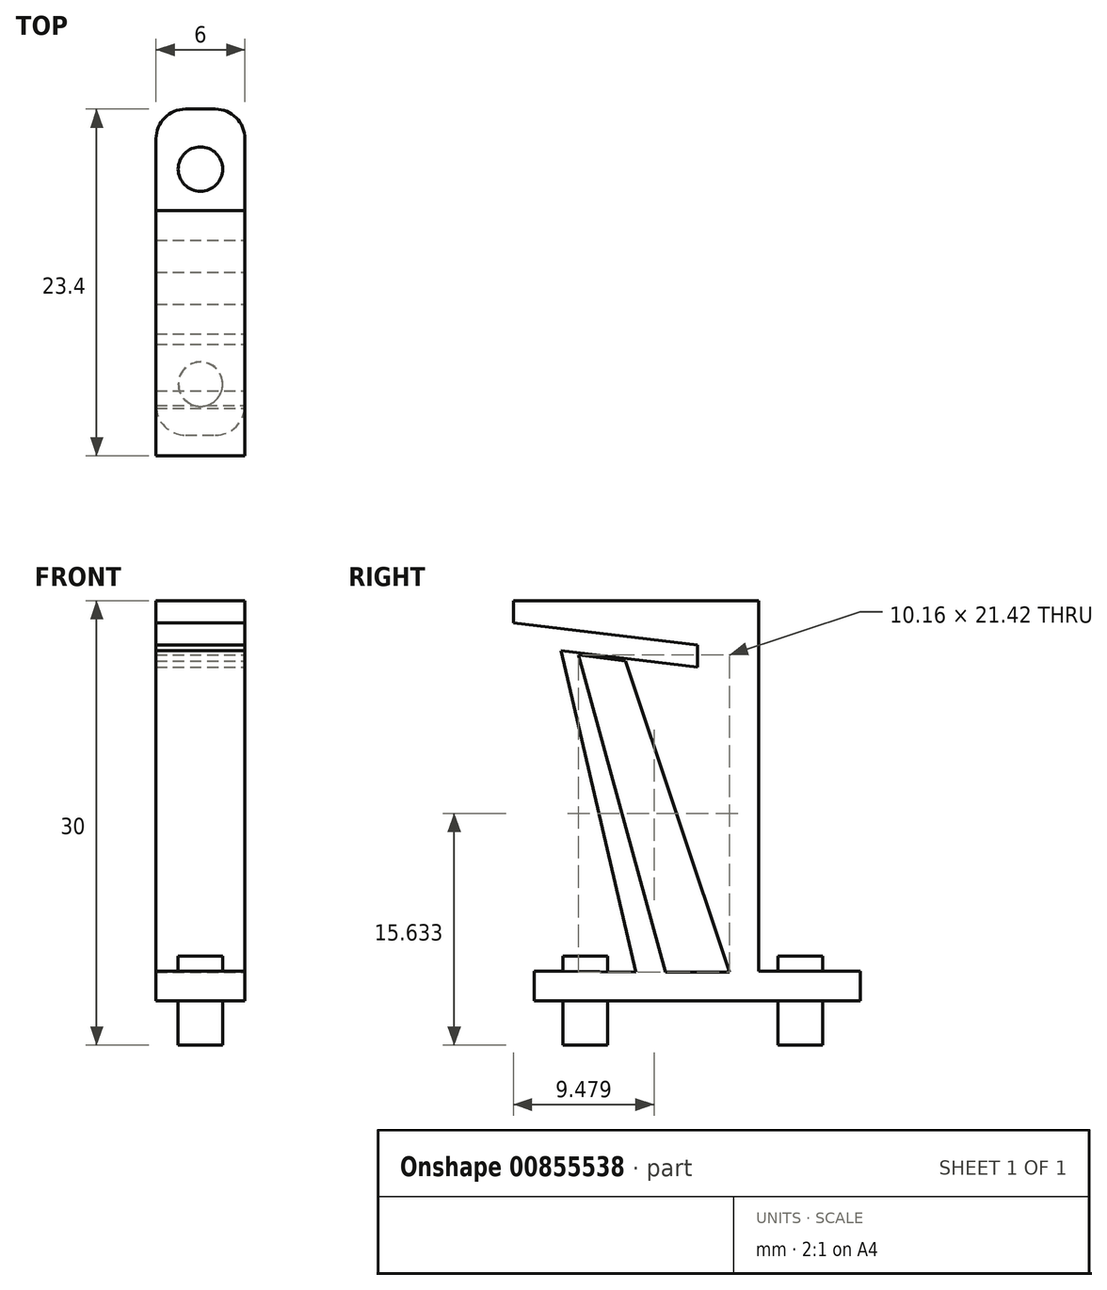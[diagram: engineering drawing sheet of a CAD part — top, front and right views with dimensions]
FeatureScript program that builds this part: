
annotation { "Feature Type Name" : "Feature", "Feature Type Description" : "" }
export const myFeature = defineFeature(function(context is Context, id is Id, definition is map)
    precondition{}
    {
        {
            var Q0;
            Q0=qCreatedBy(makeId("Top.planeOp"),FACE);
            var sketch = newSketch(context, id + "F0", { "sketchPlane" : qUnion([Q0])});
            skLineSegment(sketch, "E0.bottom", {"start": v(-3, 11) * mm, "end": v(3, 11) * mm});
            skLineSegment(sketch, "E0.top", {"start": v(-3, -11) * mm, "end": v(3, -11) * mm});
            skLineSegment(sketch, "E0.left", {"start": v(-3, 11) * mm, "end": v(-3, -11) * mm});
            skLineSegment(sketch, "E0.right", {"start": v(3, 11) * mm, "end": v(3, -11) * mm});
            skPoint(sketch, "E0.middle", {"position": v(0, 0) * mm});
            skCircle(sketch, "E1", {"center": v(0, -7.55) * mm, "radius": 1.5 * mm});
            skCircle(sketch, "E2", {"center": v(0, 6.95) * mm, "radius": 1.5 * mm});
            skSolve(sketch);
        }
        {
            var Q0;
            Q0 = qSketchRegion(id + "F0", true);
            extrude(context, id + "F1", {"entities" : qUnion([Q0]), "depth" : 2 * mm, "offsetDistance" : 25 * mm});
        }
        {
            var Q0;
            Q0=makeQuery(id+"F1.opExtrude","SWEPT_EDGE",EDGE,{"disambiguationData":[OSD([sQuery(id+"F0.wireOp",EDGE,"E0.top"),sQuery(id+"F0.wireOp",EDGE,"E0.left")])]});
            var Q1;
            Q1=makeQuery(id+"F1.opExtrude","SWEPT_EDGE",EDGE,{"disambiguationData":[OSD([sQuery(id+"F0.wireOp",EDGE,"E0.top"),sQuery(id+"F0.wireOp",EDGE,"E0.right")])]});
            var Q2;
            Q2=makeQuery(id+"F1.opExtrude","SWEPT_EDGE",EDGE,{"disambiguationData":[OSD([sQuery(id+"F0.wireOp",EDGE,"E0.bottom"),sQuery(id+"F0.wireOp",EDGE,"E0.left")])]});
            var Q3;
            Q3=makeQuery(id+"F1.opExtrude","SWEPT_EDGE",EDGE,{"disambiguationData":[OSD([sQuery(id+"F0.wireOp",EDGE,"E0.bottom"),sQuery(id+"F0.wireOp",EDGE,"E0.right")])]});
            fillet(context, id + "F2", {"entities" : qUnion([Q0, Q1, Q2, Q3]), "tangentPropagation" : true, "radius" : 2 * mm, "defaultsChanged" : true, "vertexSettings" : [], "allowEdgeOverflow" : false});
        }
        {
            var Q0;
            Q0=makeQuery(id+"F1.opExtrude","CAP_FACE",FACE,{"disambiguationData":[OSD([sQuery(id+"F0.wireOp",EDGE,"E0.bottom"),sQuery(id+"F0.wireOp",EDGE,"E0.top"),sQuery(id+"F0.wireOp",EDGE,"E0.left"),sQuery(id+"F0.wireOp",EDGE,"E0.right"),sQuery(id+"F0.wireOp",EDGE,"E1"),sQuery(id+"F0.wireOp",EDGE,"E2")])],"isStart":false});
            var sketch = newSketch(context, id + "F3", { "sketchPlane" : qUnion([Q0])});
            skLineSegment(sketch, "E3.bottom", {"start": v(-3, 4.16) * mm, "end": v(3, 4.16) * mm});
            skLineSegment(sketch, "E3.top", {"start": v(-3, -12.4) * mm, "end": v(3, -12.4) * mm});
            skLineSegment(sketch, "E3.left", {"start": v(-3, 4.16) * mm, "end": v(-3, -12.4) * mm});
            skLineSegment(sketch, "E3.right", {"start": v(3, 4.16) * mm, "end": v(3, -12.4) * mm});
            skSolve(sketch);
        }
        {
            var Q0;
            Q0 = qSketchRegion(id + "F3", true);
            extrude(context, id + "F4", {"entities" : qUnion([Q0]), "operationType" : NewBodyOperationType.ADD, "depth" : 25 * mm, "offsetDistance" : 25 * mm});
        }
        {
            var Q0;
            Q0=makeQuery(id+"F4.boolean.opBoolean","MERGE",FACE,{"derivedFrom":[makeQuery(id+"F1.opExtrude","SWEPT_FACE",FACE,{"disambiguationData":[OSD([sQuery(id+"F0.wireOp",EDGE,"E0.right")])]}),makeQuery(id+"F4.opExtrude","SWEPT_FACE",FACE,{"disambiguationData":[OSD([sQuery(id+"F3.wireOp",EDGE,"E3.right")])]})]});
            var sketch = newSketch(context, id + "F5", { "sketchPlane" : qUnion([Q0])});
            skLineSegment(sketch, "E4", {"start": v(-3.73, 22.95) * mm, "end": v(-12.4, 24) * mm});
            skLineSegment(sketch, "E5", {"start": v(-12.4, 24) * mm, "end": v(-12.4, 27) * mm});
            skLineSegment(sketch, "E6", {"start": v(-12.4, 27) * mm, "end": v(4.16, 27) * mm});
            skLineSegment(sketch, "E7", {"start": v(4.16, 27) * mm, "end": v(4.16, 22) * mm});
            skLineSegment(sketch, "E8", {"start": v(4.16, 2) * mm, "end": v(4.16, 22) * mm});
            skLineSegment(sketch, "E9", {"start": v(-4.16, 1.92) * mm, "end": v(-9, 2) * mm});
            skLineSegment(sketch, "E10", {"start": v(-9, 2) * mm, "end": v(-12.4, 2) * mm});
            skLineSegment(sketch, "E11", {"start": v(-12.4, 2) * mm, "end": v(-12.4, 24) * mm});
            skLineSegment(sketch, "E12", {"start": v(-3.73, 22.95) * mm, "end": v(4.16, 2) * mm});
            skLineSegment(sketch, "E13", {"start": v(-4.16, 1.92) * mm, "end": v(-9.19, 23.61) * mm});
            skLineSegment(sketch, "E14", {"start": v(-9.19, 23.61) * mm, "end": v(-12.4, 24) * mm});
            skLineSegment(sketch, "E15", {"start": v(-12.4, 24) * mm, "end": v(0, 22.5) * mm});
            skLineSegment(sketch, "E16", {"start": v(0, 22.5) * mm, "end": v(0, 24) * mm});
            skLineSegment(sketch, "E17", {"start": v(0, 24) * mm, "end": v(-12.4, 25.5) * mm});
            skLineSegment(sketch, "E18", {"start": v(-12.4, 25.5) * mm, "end": v(-12.4, 24) * mm});
            skSolve(sketch);
        }
        {
            var Q0;
            Q0=makeQuery(id+"F5.imprint","IMPRINT",FACE,{"disambiguationData":[TD([[makeQuery(id+"F5.imprint","IMPRINT",EDGE,{"derivedFrom":sQuery(id+"F5.wireOp",EDGE,"E9")}),-1.0]])]});
            var Q1;
            Q1=makeQuery(id+"F5.imprint","IMPRINT",FACE,{"disambiguationData":[TD([[makeQuery(id+"F5.imprint","IMPRINT",EDGE,{"derivedFrom":sQuery(id+"F5.wireOp",EDGE,"E5")}),1.0]])]});
            extrude(context, id + "F6", {"entities" : qUnion([Q0, Q1]), "operationType" : NewBodyOperationType.REMOVE, "oppositeDirection" : true, "depth" : 6 * mm, "offsetDistance" : 25 * mm});
        }
        {
            var Q0;
            Q0=makeQuery(id+"F4.boolean.opBoolean","MERGE",FACE,{"derivedFrom":[makeQuery(id+"F1.opExtrude","SWEPT_FACE",FACE,{"disambiguationData":[OSD([sQuery(id+"F0.wireOp",EDGE,"E0.right")])]}),makeQuery(id+"F4.opExtrude","SWEPT_FACE",FACE,{"disambiguationData":[OSD([sQuery(id+"F3.wireOp",EDGE,"E3.right")])]})]});
            var sketch = newSketch(context, id + "F7", { "sketchPlane" : qUnion([Q0])});
            skLineSegment(sketch, "E19", {"start": v(-2.16, 1.92) * mm, "end": v(2.16, 1.92) * mm});
            skLineSegment(sketch, "E20", {"start": v(2.16, 1.92) * mm, "end": v(-4.85, 22.9) * mm});
            skLineSegment(sketch, "E21", {"start": v(-8, 23.34) * mm, "end": v(-2.16, 1.92) * mm});
            skLineSegment(sketch, "E22", {"start": v(-8, 23.34) * mm, "end": v(-4.85, 22.9) * mm});
            skSolve(sketch);
        }
        {
            var Q0;
            Q0=makeQuery(id+"F0.imprint","IMPRINT",FACE,{"disambiguationData":[TD([[makeQuery(id+"F0.imprint","IMPRINT",EDGE,{"derivedFrom":sQuery(id+"F0.wireOp",EDGE,"E1")}),1.0]])]});
            var Q1;
            Q1=makeQuery(id+"F0.imprint","IMPRINT",FACE,{"disambiguationData":[TD([[makeQuery(id+"F0.imprint","IMPRINT",EDGE,{"derivedFrom":sQuery(id+"F0.wireOp",EDGE,"E2")}),1.0]])]});
            extrude(context, id + "F8", {"entities" : qUnion([Q0, Q1]), "operationType" : NewBodyOperationType.ADD, "oppositeDirection" : true, "depth" : 6 * mm, "offsetDistance" : 25 * mm, "symmetric" : true});
        }
        {
            var Q0;
            Q0=makeQuery(id+"F7.imprint","IMPRINT",FACE,{"disambiguationData":[TD([[makeQuery(id+"F7.imprint","IMPRINT",EDGE,{"derivedFrom":sQuery(id+"F7.wireOp",EDGE,"E19")}),1.0]])]});
            extrude(context, id + "F9", {"entities" : qUnion([Q0]), "operationType" : NewBodyOperationType.REMOVE, "oppositeDirection" : true, "depth" : 6 * mm, "offsetDistance" : 25 * mm});
        }
    });
